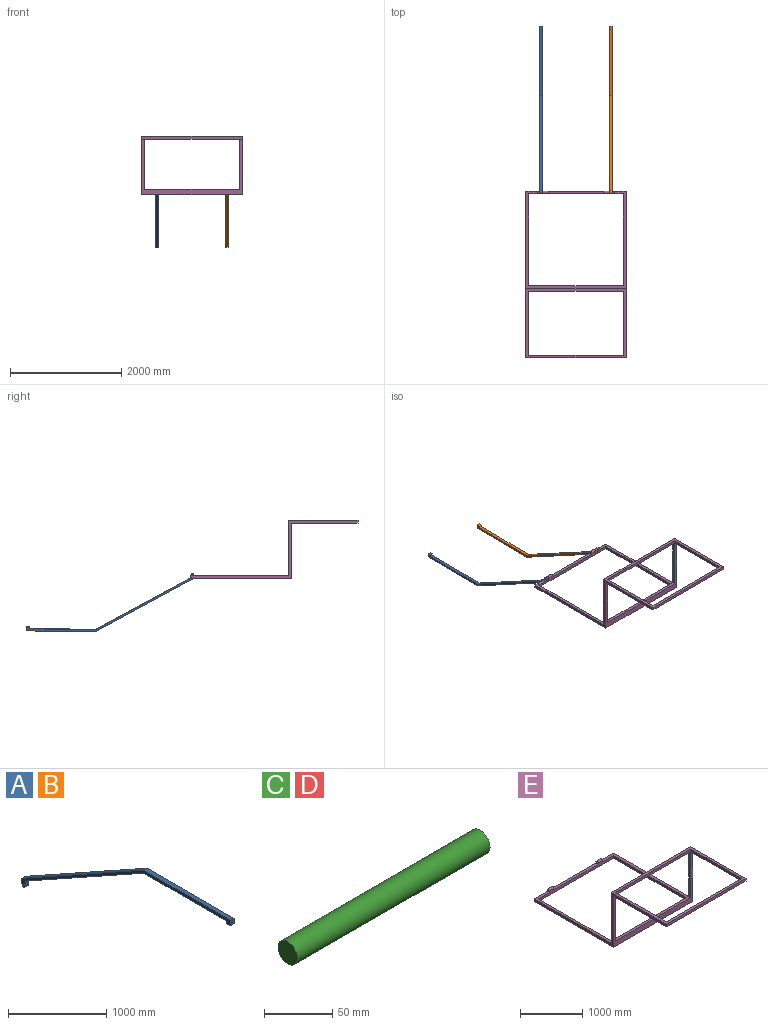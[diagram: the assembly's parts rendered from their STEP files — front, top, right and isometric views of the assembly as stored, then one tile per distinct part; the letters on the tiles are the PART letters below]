
ASSEMBLY  parts=5 mates=4
PART A: 13 faces, bbox 50x3000x1071.5 mm
  f0: plane 60x50mm, normal (0,-1,0), area 3000mm2, adj f1,f9,f11,f12
  f1: plane 1701.14x948.61mm, normal (0,-0.49,-0.87), area 97387.6mm2, adj f0,f2,f11,f12
  f2: plane 1193.86x50mm, normal (0,0,-1), area 59693.1mm2, adj f1,f3,f11,f12
  f3: plane 50x30.73mm, normal (0,1,0), area 1536.4mm2, adj f2,f4,f11,f12
  f4: plane 55x50mm, normal (0,0,-1), area 2749.8mm2, adj f3,f5,f11,f12
  f5: plane 68.61x50mm, normal (0,-1,0), area 3430.5mm2, adj f4,f6,f11,f12
  f6: plane 1248.86x50mm, normal (0,0,1), area 62443mm2, adj f5,f7,f11,f12
  f7: plane 1751.14x976.49mm, normal (0,0.49,0.87), area 100250mm2, adj f6,f8,f11,f12
  f8: plane 70x50mm, normal (0,1,0), area 3500mm2, adj f7,f9,f11,f12
  f9: cylinder r=25mm len=50mm, axis (1,0,0), area 3927mm2, adj f0,f8,f11,f12
  f10: cylinder r=10mm len=50mm, axis (1,0,0), area 3141.6mm2, adj f11,f12
  f11: plane 3000x1071.49mm, normal (-1,0,0), area 118305mm2, adj f0,f1,f2,f3,f4,f5,f6,f7
  f12: plane 3000x1071.49mm, normal (1,0,0), area 118305mm2, adj f0,f1,f2,f3,f4,f5,f6,f7
PART B: same geometry as A
PART C: 3 faces, bbox 200x20x20 mm
  f0: cylinder r=10mm len=200mm, axis (-1,0,0), area 12566.4mm2, adj f1,f2
  f1: plane 20x20mm, normal (1,0,0), area 314.2mm2, adj f0
  f2: plane 20x20mm, normal (-1,0,0), area 314.2mm2, adj f0
PART D: same geometry as C
PART E: 32 faces, bbox 1800x3000x1050 mm
  f0: plane 1000x50mm, normal (0,0,1), area 50000mm2, adj f9,f19,f24,f26
  f1: plane 1800x1800mm, normal (0,0,-1), area 435000mm2, adj f3,f9,f10,f11,f19,f20,f21,f22
  f2: plane 1800x1745mm, normal (0,0,1), area 276000mm2, adj f9,f10,f11,f19,f20,f21,f22,f23
  f3: plane 1800x1000mm, normal (0,-1,0), area 270000mm2, adj f1,f5,f10,f11,f15,f16,f18
  f4: plane 1800x995mm, normal (0,1,0), area 261000mm2, adj f6,f10,f11,f15,f16,f17,f18,f31
  f5: plane 1800x1200mm, normal (0,0,-1), area 205000mm2, adj f3,f7,f10,f11,f12,f13,f14
  f6: plane 1800x1250mm, normal (0,0,1), area 295000mm2, adj f4,f7,f8,f10,f11,f12,f13,f14
  f7: plane 1800x50mm, normal (0,-1,0), area 90000mm2, adj f5,f6,f10,f11
  f8: plane 1700x50mm, normal (0,-1,0), area 85000mm2, adj f6,f12,f13,f17
  f9: plane 1800x75mm, normal (0,1,0), area 95000mm2, adj f0,f1,f2,f10,f11,f23,f24,f25
  f10: plane 3000x1050mm, normal (1,0,0), area 200005.4mm2, adj f1,f2,f3,f4,f5,f6,f7,f9
  f11: plane 3000x1050mm, normal (-1,0,0), area 200005.4mm2, adj f1,f2,f3,f4,f5,f6,f7,f9
  f12: plane 1150x50mm, normal (-1,0,0), area 57500mm2, adj f5,f6,f8,f14
  f13: plane 1150x50mm, normal (1,0,0), area 57500mm2, adj f5,f6,f8,f14
  f14: plane 1700x50mm, normal (0,1,0), area 85000mm2, adj f5,f6,f12,f13
  f15: plane 1700x50mm, normal (0,0,1), area 85000mm2, adj f3,f4,f16,f18
  f16: plane 900x50mm, normal (1,0,0), area 45000mm2, adj f3,f4,f15,f17
  f17: plane 1700x50mm, normal (0,0,-1), area 85000mm2, adj f4,f8,f16,f18
  f18: plane 900x50mm, normal (-1,0,0), area 45000mm2, adj f3,f4,f15,f17
  f19: plane 1700x75mm, normal (0,-1,0), area 90000mm2, adj f0,f1,f2,f20,f22,f23,f24,f25
  f20: plane 1650x50mm, normal (1,0,0), area 82500mm2, adj f1,f2,f19,f21
  f21: plane 1700x50mm, normal (0,1,0), area 85000mm2, adj f1,f2,f20,f22
  f22: plane 1650x50mm, normal (-1,0,0), area 82500mm2, adj f1,f2,f19,f21
  f23: plane 50x50mm, normal (1,0,0), area 1917.6mm2, adj f2,f9,f19,f28,f30
  f24: plane 50x50mm, normal (-1,0,0), area 1917.6mm2, adj f0,f9,f19,f28,f30
  f25: plane 50x50mm, normal (-1,0,0), area 1917.6mm2, adj f2,f9,f19,f27,f29
  f26: plane 50x50mm, normal (1,0,0), area 1917.6mm2, adj f0,f9,f19,f27,f29
  f27: cylinder r=25mm len=100mm, axis (1,0,0), area 7854mm2, adj f9,f19,f25,f26
  f28: cylinder r=25mm len=100mm, axis (1,0,0), area 7854mm2, adj f9,f19,f23,f24
  f29: cylinder r=10mm len=100mm, axis (-1,0,0), area 6283.2mm2, adj f25,f26
  f30: cylinder r=10mm len=100mm, axis (-1,0,0), area 6283.2mm2, adj f23,f24
  f31: cylinder r=5mm len=1800mm, axis (1,0,0), area 14137.2mm2, adj f2,f4,f10,f11
PLACE A rot(axis=(-1,0,0),179.3deg) t=(337.58,5178.19,-1335.84)mm
PLACE B rot(axis=(-1,0,0),179.2deg) t=(1587.58,5180.34,-1328.6)mm
PLACE C t=(237.58,-782.27,479.81)mm
PLACE D t=(-962.42,-782.27,479.81)mm
PLACE E t=(337.58,-782.27,479.81)mm fixed
MATE fastened E.f27 <-> C.f0  axis (-1,0,0) through (1737.58,2192.73,-445.19)mm
MATE revolute B.f9 <-> E.f27  axis (-1,0,0) through (1837.58,2192.73,-445.19)mm
MATE revolute A.f9 <-> E.f27  axis (1,0,0) through (637.58,2192.73,-445.19)mm
MATE fastened E.f27 <-> D.f0  axis (1,0,0) through (737.58,2192.73,-445.19)mm
